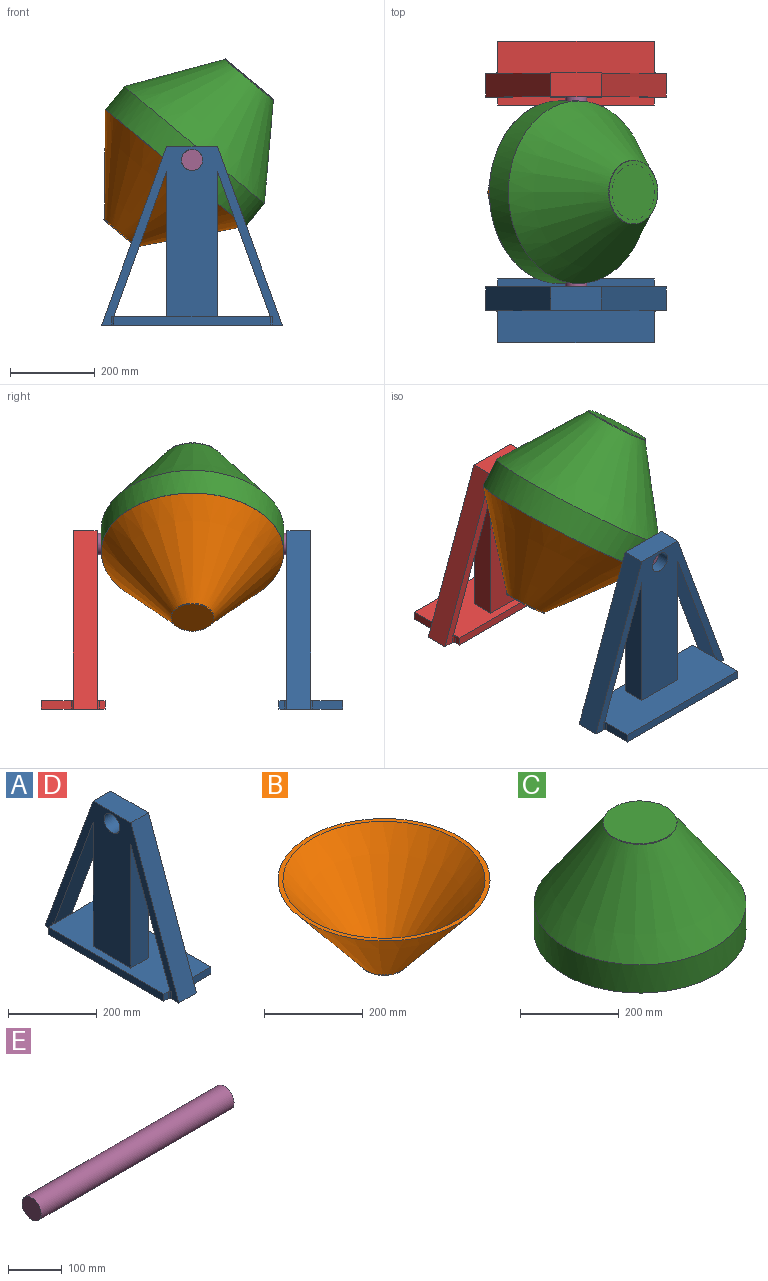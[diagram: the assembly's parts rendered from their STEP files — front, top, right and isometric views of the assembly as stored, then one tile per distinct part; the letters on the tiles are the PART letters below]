
ASSEMBLY  parts=5 mates=2
PART A: 22 faces, bbox 150x425.7x420 mm
  f0: plane 378.61x150mm, normal (0,0,1), area 48592.8mm2, adj f1,f5,f6,f7,f10,f11,f12,f13
  f1: plane 341.52x56mm, normal (0,1,0), area 19125.3mm2, adj f0,f7,f10,f11
  f2: plane 120x56mm, normal (0,0,1), area 6720mm2, adj f3,f8,f10,f11
  f3: plane 420x152.87mm, normal (0,-0.94,0.34), area 25029.5mm2, adj f2,f4,f10,f11
  f4: plane 425.74x150mm, normal (0,0,-1), area 58511.9mm2, adj f3,f8,f10,f11,f12,f13,f14,f15
  f5: plane 341.52x124.3mm, normal (0,0.94,-0.34), area 20352.8mm2, adj f0,f6,f10,f11
  f6: plane 341.52x56mm, normal (0,-1,0), area 19125.3mm2, adj f0,f5,f10,f11
  f7: plane 341.52x124.3mm, normal (0,-0.94,-0.34), area 20352.8mm2, adj f0,f1,f10,f11
  f8: plane 420x152.87mm, normal (0,0.94,0.34), area 25029.5mm2, adj f2,f4,f10,f11
  f9: cylinder r=25mm len=56mm, axis (-1,0,0), area 8796.5mm2, adj f10,f11
  f10: plane 425.74x420mm, normal (1,0,0), area 62615.7mm2, adj f0,f1,f2,f3,f4,f5,f6,f7
  f11: plane 425.74x420mm, normal (-1,0,0), area 62615.7mm2, adj f0,f1,f2,f3,f4,f5,f6,f7
  f12: plane 368.61x20mm, normal (-1,0,0), area 7372.2mm2, adj f0,f4,f13,f14
  f13: plane 20x14mm, normal (0,-1,0), area 280mm2, adj f0,f4,f12,f20
  f14: plane 20x14mm, normal (0,1,0), area 280mm2, adj f0,f4,f12,f21
  f15: plane 70x20mm, normal (0,-1,0), area 1400mm2, adj f0,f4,f17,f18
  f16: plane 70x20mm, normal (0,1,0), area 1400mm2, adj f0,f4,f17,f19
  f17: plane 368.61x20mm, normal (1,0,0), area 7372.2mm2, adj f0,f4,f15,f16
  f18: cylinder r=5mm len=20mm, axis (0,0,1), area 157.1mm2, adj f0,f4,f10,f15
  f19: cylinder r=5mm len=20mm, axis (0,0,-1), area 157.1mm2, adj f0,f4,f10,f16
  f20: cylinder r=5mm len=20mm, axis (0,0,-1), area 157.1mm2, adj f0,f4,f11,f13
  f21: cylinder r=5mm len=20mm, axis (0,0,1), area 157.1mm2, adj f0,f4,f11,f14
PART B: 6 faces, bbox 430x430x202 mm
  f0: plane 430x430mm, normal (0,0,1), area 13194.7mm2, adj f1,f2
  f1: cone r=205mm half-angle=39.5deg, axis (0,0,1), area 199563.6mm2, adj f0,f3
  f2: cone r=215mm half-angle=39.5deg, axis (0,0,1), area 215854.5mm2, adj f0,f4
  f3: plane 80x80mm, normal (0,0,1), area 5026.5mm2, adj f1
  f4: cylinder r=50mm len=100mm, axis (0,0,1), area 628.3mm2, adj f2,f5
  f5: plane 100x100mm, normal (0,0,-1), area 7854mm2, adj f4
PART C: 8 faces, bbox 430x430x272 mm
  f0: cone r=65mm half-angle=35deg, axis (0,0,-1), area 207079.3mm2, adj f2,f5
  f1: cone r=75mm half-angle=35deg, axis (0,0,-1), area 222418.5mm2, adj f3,f6
  f2: cylinder r=205mm len=410mm, axis (0,0,1), area 90163.7mm2, adj f0,f4
  f3: cylinder r=215mm len=430mm, axis (0,0,1), area 94561.9mm2, adj f1,f4
  f4: plane 430x430mm, normal (0,0,-1), area 13194.7mm2, adj f2,f3
  f5: plane 130x130mm, normal (0,0,-1), area 13273.2mm2, adj f0
  f6: cylinder r=75mm len=150mm, axis (0,0,-1), area 942.5mm2, adj f1,f7
  f7: plane 150x150mm, normal (0,0,1), area 17671.5mm2, adj f6
PART D: same geometry as A
PART E: 3 faces, bbox 506x50x50 mm
  f0: cylinder r=25mm len=506mm, axis (1,0,0), area 79482.3mm2, adj f1,f2
  f1: plane 50x50mm, normal (-1,0,0), area 1963.5mm2, adj f0
  f2: plane 50x50mm, normal (1,0,0), area 1963.5mm2, adj f0
PLACE A rot(axis=(0,0,-1),90deg) t=(578.5,1186.02,194.65)mm
PLACE B rot(axis=(0,1,0),40deg) t=(539.13,1035.26,144.99)mm
PLACE C rot(axis=(0,1,0),40deg) t=(584.09,1035.26,198.64)mm
PLACE D rot(axis=(0,0,1),90deg) t=(578.5,887.02,194.65)mm
PLACE E rot(axis=(-0.32,0.32,-0.89),96.7deg) t=(598.55,1044.02,187.36)mm
MATE fastened B.f1 <-> C.f3  axis (0.64,0,0.77) through (539.13,1035.26,144.99)mm
MATE revolute E.f0 <-> A.f9  axis (0,-1,0) through (578.5,785.02,163.43)mm
